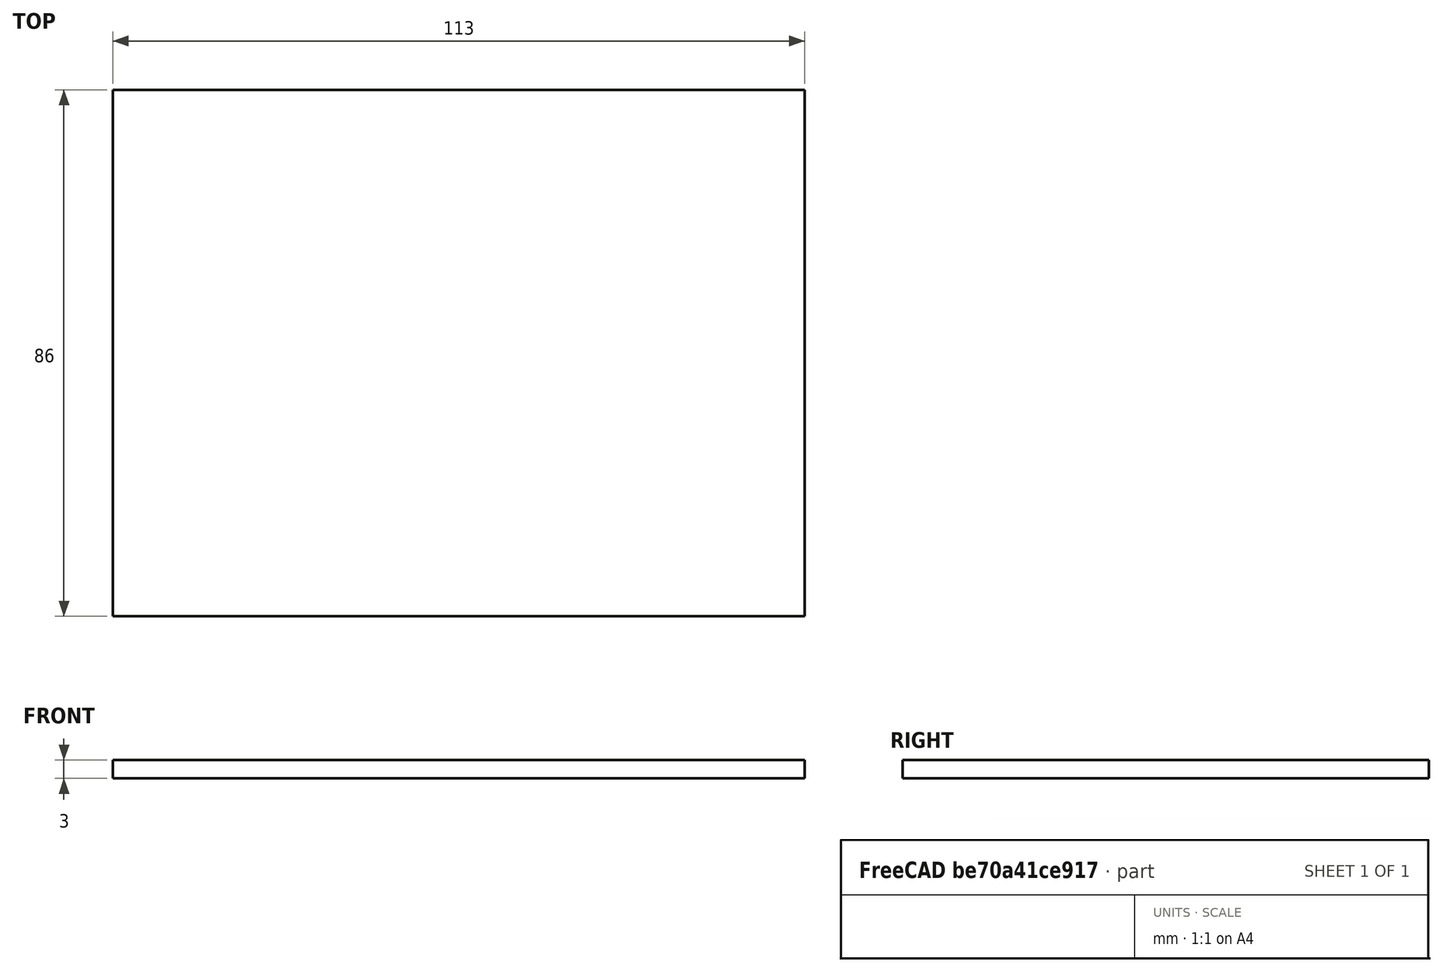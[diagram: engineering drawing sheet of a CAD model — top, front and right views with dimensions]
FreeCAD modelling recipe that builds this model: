
FCSTD DOCUMENT  (FreeCAD 0.21R33668 +7 (Git))
Label: Screen
License: All rights reserved
LicenseURL: https://en.wikipedia.org/wiki/All_rights_reserved
objects: Sketcher::SketchObject×1, PartDesign::Pad×1, PartDesign::Body×1
note: 4 computed .brp shape members not serialized (recipe doc carries the construction recipe); baked Part::Feature solids carry a one-line shape summary decoded from their .brp

FEATURE [Sketcher::SketchObject] Sketch
  FullyConstrained = true
  MapMode = 5
  Support = -> [XY_Plane]
  sketch-geometry (4):
    g0: LineSegment StartX=-56.5 StartY=-43 StartZ=0 EndX=56.5 EndY=-43 EndZ=0
    g1: LineSegment StartX=56.5 StartY=-43 StartZ=0 EndX=56.5 EndY=43 EndZ=0
    g2: LineSegment StartX=56.5 StartY=43 StartZ=0 EndX=-56.5 EndY=43 EndZ=0
    g3: LineSegment StartX=-56.5 StartY=43 StartZ=0 EndX=-56.5 EndY=-43 EndZ=0
  constraints (12):
    c: Coincident(g0,g1)
    c: Coincident(g1,g2)
    c: Coincident(g2,g3)
    c: Coincident(g3,g0)
    c: Horizontal(g0)
    c: Horizontal(g2)
    c: Vertical(g1)
    c: Vertical(g3)
    c: Symmetric(g1,g2,g-2)
    c: Symmetric(g0,g2,g-1)
    c: DistanceX(g0,g0) = 113
    c: DistanceY(g1,g1) = 86
FEATURE [PartDesign::Pad] Pad
  Direction = (0,0,1)
  Length = 3
  Length2 = 10
  Profile = -> Sketch
  ReferenceAxis = -> Sketch [N_Axis]
  Type = 0
FEATURE [PartDesign::Body] Body
  Group = -> [Sketch,Pad]
  Origin = -> Origin
  Tip = -> Pad
